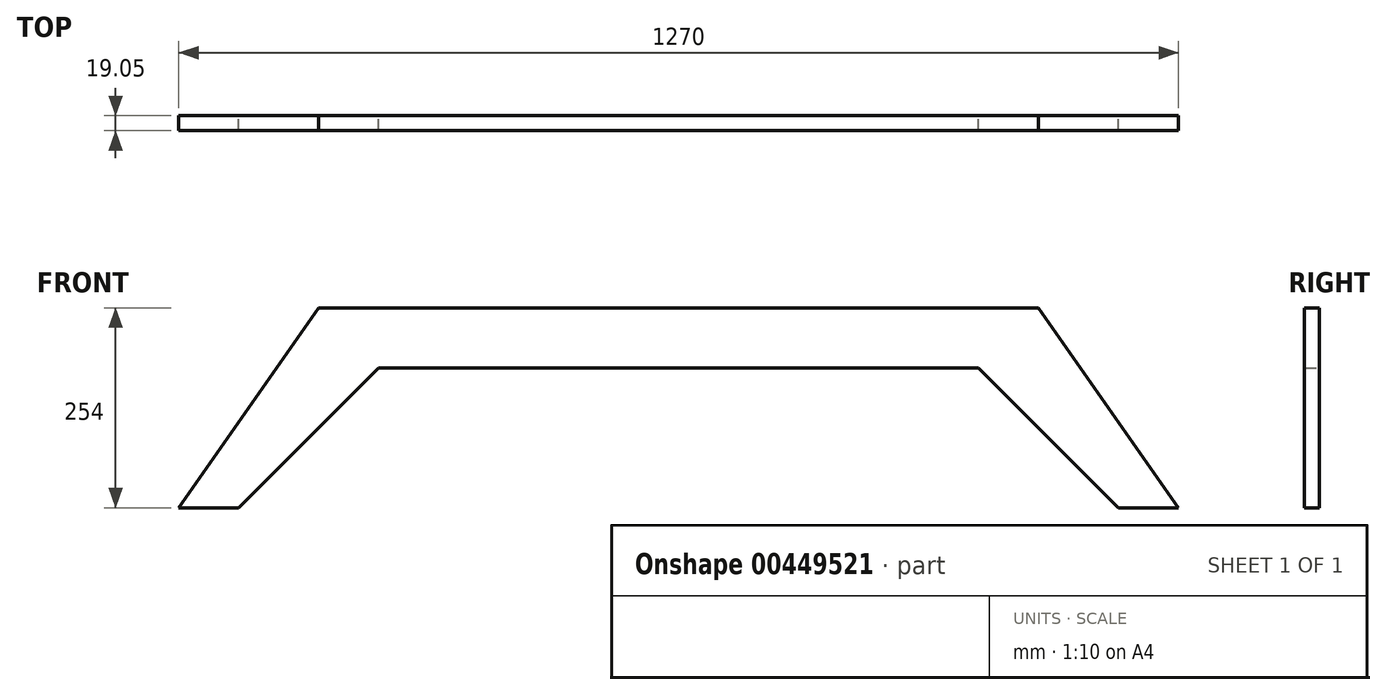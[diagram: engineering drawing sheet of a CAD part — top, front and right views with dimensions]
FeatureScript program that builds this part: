
annotation { "Feature Type Name" : "Feature", "Feature Type Description" : "" }
export const myFeature = defineFeature(function(context is Context, id is Id, definition is map)
    precondition{}
    {
        {
            var Q0;
            Q0=qCreatedBy(makeId("Front.planeOp"),FACE);
            var sketch = newSketch(context, id + "F0", { "sketchPlane" : qUnion([Q0])});
            skLineSegment(sketch, "E0", {"start": v(0, 0) * mm, "end": v(457.15, 0) * mm});
            skLineSegment(sketch, "E1", {"start": v(457.15, 0) * mm, "end": v(635, -254) * mm});
            skLineSegment(sketch, "E2", {"start": v(635, -254) * mm, "end": v(558.8, -254) * mm});
            skLineSegment(sketch, "E3", {"start": v(558.8, -254) * mm, "end": v(381, -76.2) * mm});
            skLineSegment(sketch, "E4", {"start": v(381, -76.2) * mm, "end": v(0, -76.2) * mm});
            skLineSegment(sketch, "E5.MirrorCS", {"start": v(0, 0) * mm, "end": v(-457.15, 0) * mm});
            skLineSegment(sketch, "E6.MirrorCS", {"start": v(-381, -76.2) * mm, "end": v(0, -76.2) * mm});
            skLineSegment(sketch, "E7.MirrorCS", {"start": v(-635, -254) * mm, "end": v(-558.8, -254) * mm});
            skLineSegment(sketch, "E8.MirrorCS", {"start": v(-457.15, 0) * mm, "end": v(-635, -254) * mm});
            skLineSegment(sketch, "E9.MirrorCS", {"start": v(-558.8, -254) * mm, "end": v(-381, -76.2) * mm});
            skLineSegment(sketch, "E10", {"start": v(381, -76.2) * mm, "end": v(457.15, 0) * mm, "construction": true});
            skSolve(sketch);
        }
        {
            var Q0;
            Q0=makeQuery(id+"F0.imprint","IMPRINT",FACE,{"disambiguationData":[TD([[makeQuery(id+"F0.imprint","IMPRINT",EDGE,{"derivedFrom":sQuery(id+"F0.wireOp",EDGE,"E0")}),-1.0]])]});
            extrude(context, id + "F1", {"entities" : qUnion([Q0]), "depth" : 19.05 * mm});
        }
    });
